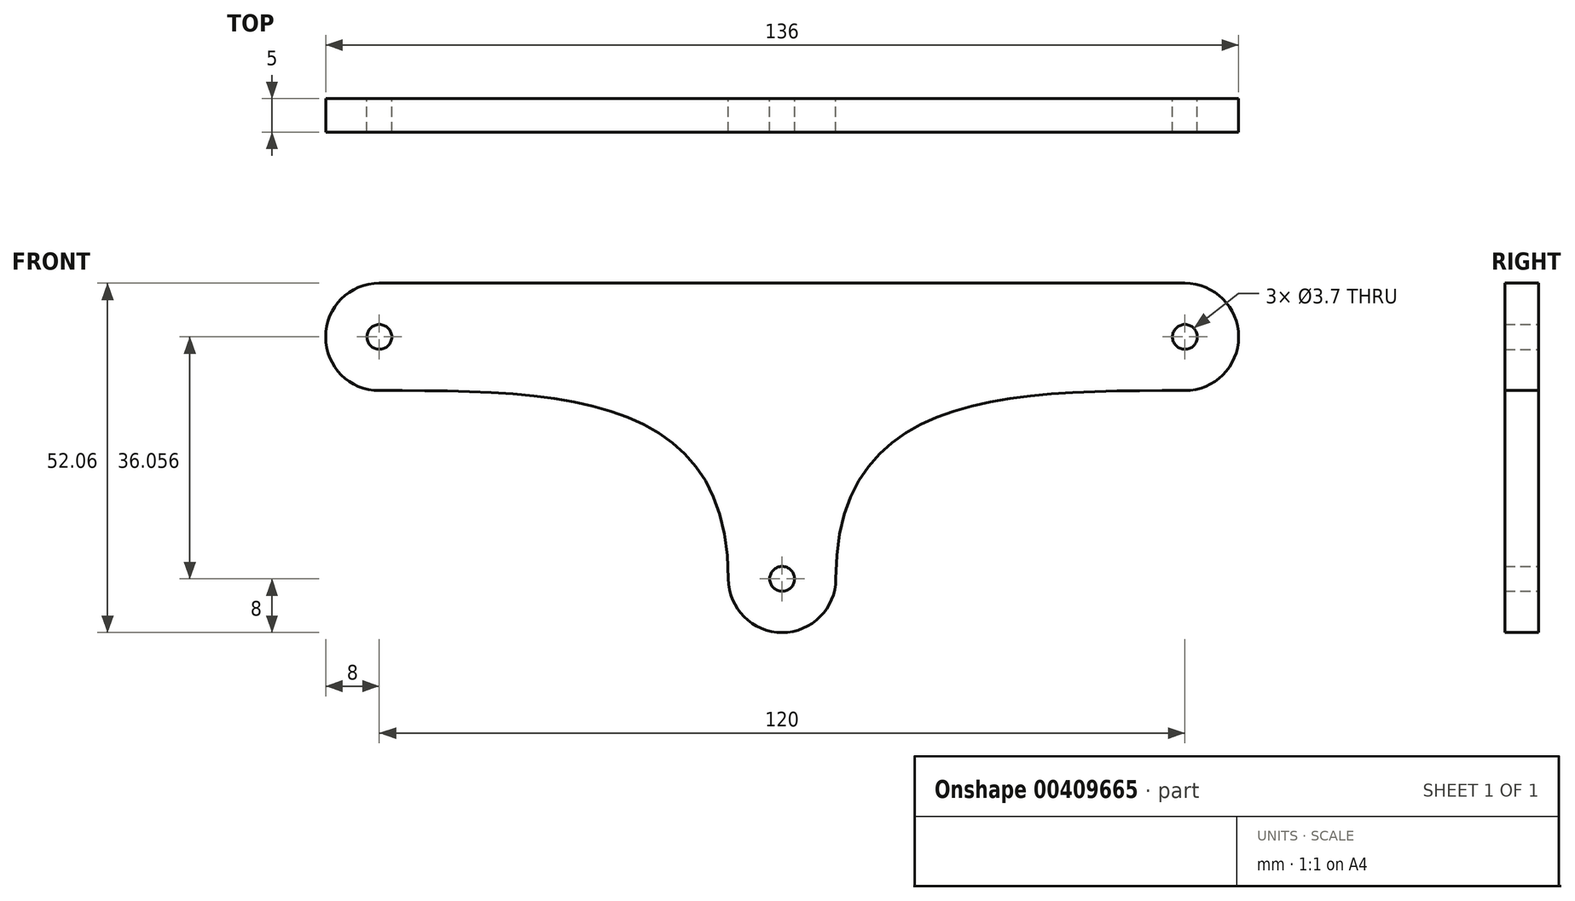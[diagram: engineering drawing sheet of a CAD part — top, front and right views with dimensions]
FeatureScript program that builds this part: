
annotation { "Feature Type Name" : "Feature", "Feature Type Description" : "" }
export const myFeature = defineFeature(function(context is Context, id is Id, definition is map)
    precondition{}
    {
        {
            var Q0;
            Q0=qCreatedBy(makeId("Front.planeOp"),FACE);
            var sketch = newSketch(context, id + "F0", { "sketchPlane" : qUnion([Q0])});
            skCircle(sketch, "E0", {"center": v(-60, 36.06) * mm, "radius": 1.85 * mm});
            skCircle(sketch, "E1", {"center": v(0, 0) * mm, "radius": 1.85 * mm});
            skCircle(sketch, "E2", {"center": v(60, 36.06) * mm, "radius": 1.85 * mm});
            skCircle(sketch, "E3", {"center": v(-60, 36.06) * mm, "radius": 8 * mm});
            skCircle(sketch, "E4", {"center": v(60, 36.06) * mm, "radius": 8 * mm});
            skCircle(sketch, "E5", {"center": v(0, 0) * mm, "radius": 8 * mm});
            skLineSegment(sketch, "E6", {"start": v(-60, 44.06) * mm, "end": v(60, 44.06) * mm});
            skFitSpline(sketch, "E7", {"points": [v(-60, 28.06) * mm, v(-8, 0) * mm], "startDerivative": vector(78, 0) * mm, "endDerivative": vector(0, -84.17) * mm});
            skFitSpline(sketch, "E8.MirrorCS", {"points": [v(60, 28.06) * mm, v(8, 0) * mm], "startDerivative": vector(-78, 0) * mm, "endDerivative": vector(0, -84.17) * mm});
            skSolve(sketch);
        }
        {
            var Q0;
            {var subQ3=sQuery(id+"F0.wireOp",EDGE,"E6");Q0=makeQuery(id+"F0.imprint","IMPRINT",FACE,{"disambiguationData":[TD([[makeQuery(id+"F0.imprint","IMPRINT",EDGE,{"derivedFrom":subQ3}),-1.0]])]});}
            var Q1;
            Q1=makeQuery(id+"F0.imprint","IMPRINT",FACE,{"disambiguationData":[TD([[makeQuery(id+"F0.imprint","IMPRINT",EDGE,{"derivedFrom":sQuery(id+"F0.wireOp",EDGE,"E0")}),-1.0]])]});
            var Q2;
            Q2=makeQuery(id+"F0.imprint","IMPRINT",FACE,{"disambiguationData":[TD([[makeQuery(id+"F0.imprint","IMPRINT",EDGE,{"derivedFrom":sQuery(id+"F0.wireOp",EDGE,"E1")}),-1.0]])]});
            var Q3;
            Q3=makeQuery(id+"F0.imprint","IMPRINT",FACE,{"disambiguationData":[TD([[makeQuery(id+"F0.imprint","IMPRINT",EDGE,{"derivedFrom":sQuery(id+"F0.wireOp",EDGE,"E2")}),-1.0]])]});
            extrude(context, id + "F1", {"entities" : qUnion([Q0, Q1, Q2, Q3]), "endBound" : BoundingType.SYMMETRIC, "depth" : 5 * mm});
        }
    });
